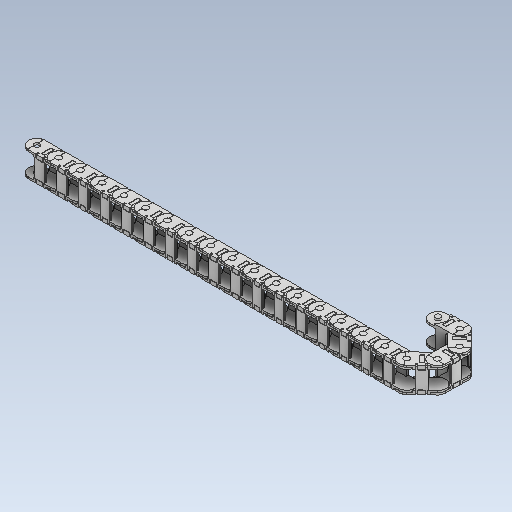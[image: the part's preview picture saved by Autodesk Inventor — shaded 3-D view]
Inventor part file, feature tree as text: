
AUTODESK INVENTOR PART (.ipt)
format: ipt  version: 2020 (Build 240168000, 168)  size: 2,507,776 bytes
history: native  units: in
note: dims shown in document units (in); Inventor stores cm internally (conversion verified against a paired STEP export)
features: other x20, mirror x1
ambient origin geometry x8: Origin, YZ Plane, XZ Plane, XY Plane, X Axis, Y Axis, Z Axis, Center Point
bodies: Solid1 (feature_tree), Solid2 (feature_tree), Solid3 (feature_tree), Solid4 (feature_tree), Solid5 (feature_tree), Solid6 (feature_tree), Solid7 (feature_tree), Solid8 (feature_tree), Solid9 (feature_tree), Solid10 (feature_tree), Solid11 (feature_tree), Solid12 (feature_tree), Solid13 (feature_tree), Solid14 (feature_tree), Solid15 (feature_tree), Solid16 (feature_tree), Solid17 (feature_tree), Solid18 (feature_tree), Solid19 (feature_tree), Solid20 (feature_tree), Solid21 (feature_tree)
feature tree (21):
  other  "CirPattern1[1]"
  other  "CirPattern1[2]"
  other  "CirPattern1[3]"
  other  "LPattern1[1]"
  other  "LPattern1[2]"
  other  "LPattern1[3]"
  other  "LPattern1[4]"
  other  "LPattern1[5]"
  other  "LPattern1[6]"
  other  "LPattern1[7]"
  other  "LPattern1[8]"
  other  "LPattern1[9]"
  other  "LPattern1[10]"
  other  "LPattern1[11]"
  other  "LPattern1[12]"
  other  "LPattern1[13]"
  other  "LPattern1[14]"
  other  "LPattern1[15]"
  other  "LPattern1[16]"
  other  "Body-Move_Copy1"
  mirror  "Mirror1"
